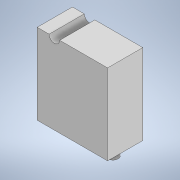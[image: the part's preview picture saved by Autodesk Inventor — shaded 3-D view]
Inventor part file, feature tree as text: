
AUTODESK INVENTOR PART (.ipt)
format: ipt  version: 2021 (Build 250183000, 183)  size: 111,616 bytes
history: native  units: mm
features: extrude x3, sketch x3
ambient origin geometry x8: Origin, YZ Plane, XZ Plane, XY Plane, X Axis, Y Axis, Z Axis, Center Point
bodies: Solid1 (feature_tree)
feature tree (6):
  extrude  "Extrusion1"  Depth=22.877mm
  extrude  "Extrusion2"  Depth=10.0mm
  extrude  "Extrusion3"  Depth=3.0mm
  sketch  "Sketch1"  dims[d0=22.877mm d1=11.4385mm]
  sketch  "Sketch2"  dims[d3=10.0mm d4=5.0mm]
  sketch  "Sketch3"  dims[d5=20.0mm d6=0.0mm d7=3.0mm d8=3.5mm d9=3.0mm d10=0.0mm d11=3.0mm d12=4.887mm d13=0.0mm d14=0.0mm]
